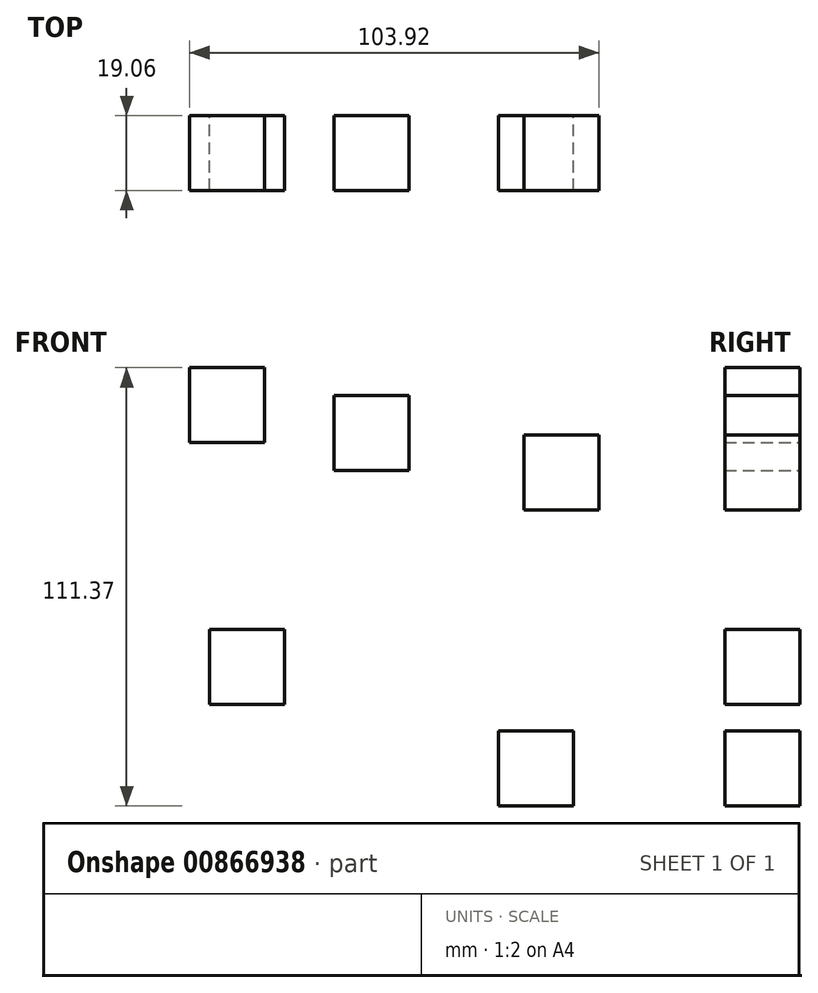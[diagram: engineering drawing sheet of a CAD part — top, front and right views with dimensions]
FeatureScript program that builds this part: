
annotation { "Feature Type Name" : "Feature", "Feature Type Description" : "" }
export const myFeature = defineFeature(function(context is Context, id is Id, definition is map)
    precondition{}
    {
        {
            var Q0;
            Q0=qCreatedBy(makeId("Front.planeOp"),FACE);
            var sketch = newSketch(context, id + "F0", { "sketchPlane" : qUnion([Q0])});
            skLineSegment(sketch, "E0.bottom", {"start": v(-37.88, 40.09) * mm, "end": v(-56.93, 40.09) * mm});
            skLineSegment(sketch, "E0.top", {"start": v(-37.88, 59.14) * mm, "end": v(-56.93, 59.14) * mm});
            skLineSegment(sketch, "E0.left", {"start": v(-37.88, 40.09) * mm, "end": v(-37.88, 59.14) * mm});
            skLineSegment(sketch, "E0.right", {"start": v(-56.93, 40.09) * mm, "end": v(-56.93, 59.14) * mm});
            skPoint(sketch, "E0.middle", {"position": v(-47.4, 49.61) * mm});
            skLineSegment(sketch, "E1.bottom", {"start": v(-1.28, 32.96) * mm, "end": v(-20.33, 32.96) * mm});
            skLineSegment(sketch, "E1.top", {"start": v(-1.28, 52) * mm, "end": v(-20.33, 52) * mm});
            skLineSegment(sketch, "E1.left", {"start": v(-1.28, 32.96) * mm, "end": v(-1.28, 52) * mm});
            skLineSegment(sketch, "E1.right", {"start": v(-20.33, 32.96) * mm, "end": v(-20.33, 52) * mm});
            skPoint(sketch, "E1.middle", {"position": v(-10.8, 42.48) * mm});
            skLineSegment(sketch, "E2.bottom", {"start": v(46.99, 22.92) * mm, "end": v(27.94, 22.92) * mm});
            skLineSegment(sketch, "E2.top", {"start": v(46.99, 41.97) * mm, "end": v(27.94, 41.97) * mm});
            skLineSegment(sketch, "E2.left", {"start": v(46.99, 22.92) * mm, "end": v(46.99, 41.97) * mm});
            skLineSegment(sketch, "E2.right", {"start": v(27.94, 22.92) * mm, "end": v(27.94, 41.97) * mm});
            skPoint(sketch, "E2.middle", {"position": v(37.46, 32.44) * mm});
            skLineSegment(sketch, "E3.bottom", {"start": v(-32.86, -26.48) * mm, "end": v(-51.9, -26.48) * mm});
            skLineSegment(sketch, "E3.top", {"start": v(-32.86, -7.43) * mm, "end": v(-51.9, -7.43) * mm});
            skLineSegment(sketch, "E3.left", {"start": v(-32.86, -26.48) * mm, "end": v(-32.86, -7.43) * mm});
            skLineSegment(sketch, "E3.right", {"start": v(-51.9, -26.48) * mm, "end": v(-51.9, -7.43) * mm});
            skPoint(sketch, "E3.middle", {"position": v(-42.38, -16.96) * mm});
            skLineSegment(sketch, "E4.bottom", {"start": v(40.51, -52.23) * mm, "end": v(21.46, -52.23) * mm});
            skLineSegment(sketch, "E4.top", {"start": v(40.51, -33.18) * mm, "end": v(21.46, -33.18) * mm});
            skLineSegment(sketch, "E4.left", {"start": v(40.51, -52.23) * mm, "end": v(40.51, -33.18) * mm});
            skLineSegment(sketch, "E4.right", {"start": v(21.46, -52.23) * mm, "end": v(21.46, -33.18) * mm});
            skPoint(sketch, "E4.middle", {"position": v(30.99, -42.7) * mm});
            skSolve(sketch);
        }
        {
            var Q0;
            Q0=makeQuery(id+"F0.imprint","IMPRINT",FACE,{"disambiguationData":[TD([[makeQuery(id+"F0.imprint","IMPRINT",EDGE,{"derivedFrom":sQuery(id+"F0.wireOp",EDGE,"E0.bottom")}),-1.0]])]});
            var Q1;
            Q1=makeQuery(id+"F0.imprint","IMPRINT",FACE,{"disambiguationData":[TD([[makeQuery(id+"F0.imprint","IMPRINT",EDGE,{"derivedFrom":sQuery(id+"F0.wireOp",EDGE,"E1.bottom")}),-1.0]])]});
            var Q2;
            Q2=makeQuery(id+"F0.imprint","IMPRINT",FACE,{"disambiguationData":[TD([[makeQuery(id+"F0.imprint","IMPRINT",EDGE,{"derivedFrom":sQuery(id+"F0.wireOp",EDGE,"E2.bottom")}),-1.0]])]});
            var Q3;
            Q3=makeQuery(id+"F0.imprint","IMPRINT",FACE,{"disambiguationData":[TD([[makeQuery(id+"F0.imprint","IMPRINT",EDGE,{"derivedFrom":sQuery(id+"F0.wireOp",EDGE,"E3.bottom")}),-1.0]])]});
            var Q4;
            Q4=makeQuery(id+"F0.imprint","IMPRINT",FACE,{"disambiguationData":[TD([[makeQuery(id+"F0.imprint","IMPRINT",EDGE,{"derivedFrom":sQuery(id+"F0.wireOp",EDGE,"E4.bottom")}),-1.0]])]});
            extrude(context, id + "F1", {"entities" : qUnion([Q0, Q1, Q2, Q3, Q4]), "endBound" : BoundingType.SYMMETRIC, "depth" : 19.05 * mm, "offsetDistance" : 25.4 * mm});
        }
    });
